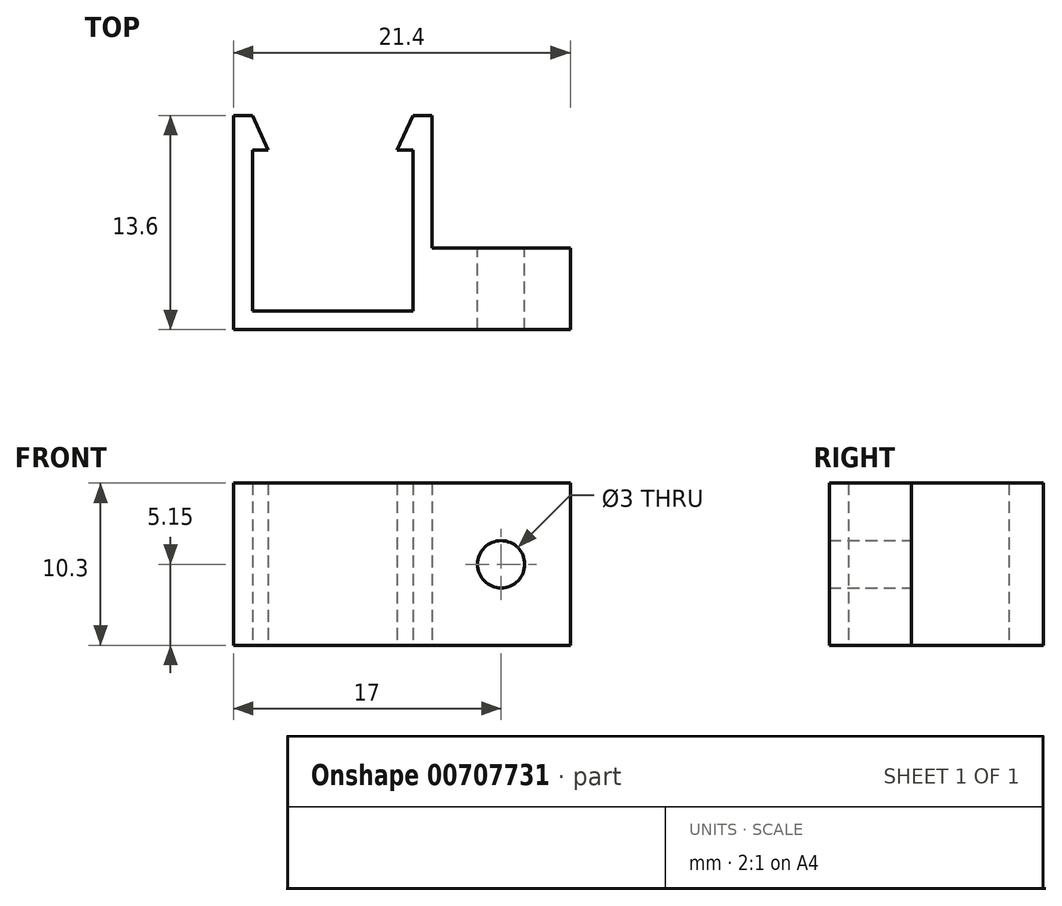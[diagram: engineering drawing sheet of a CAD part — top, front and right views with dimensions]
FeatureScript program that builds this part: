
annotation { "Feature Type Name" : "Feature", "Feature Type Description" : "" }
export const myFeature = defineFeature(function(context is Context, id is Id, definition is map)
    precondition{}
    {
        {
            var Q0;
            Q0=qCreatedBy(makeId("Top.planeOp"),FACE);
            var sketch = newSketch(context, id + "F0", { "sketchPlane" : qUnion([Q0])});
            skLineSegment(sketch, "E0.bottom", {"start": v(0, 0) * mm, "end": v(10.2, 0) * mm});
            skLineSegment(sketch, "E0.top", {"start": v(0, 10.2) * mm, "end": v(1, 10.2) * mm});
            skLineSegment(sketch, "E0.left", {"start": v(0, 0) * mm, "end": v(0, 10.2) * mm});
            skLineSegment(sketch, "E0.right", {"start": v(10.2, 0) * mm, "end": v(10.2, 10.2) * mm});
            skLineSegment(sketch, "E1.bottom", {"start": v(-1.2, 12.4) * mm, "end": v(0, 12.4) * mm});
            skLineSegment(sketch, "E1.top", {"start": v(-1.2, -1.2) * mm, "end": v(11.4, -1.2) * mm});
            skLineSegment(sketch, "E1.left", {"start": v(-1.2, 12.4) * mm, "end": v(-1.2, -1.2) * mm});
            skLineSegment(sketch, "E1.right", {"start": v(11.4, 12.4) * mm, "end": v(11.4, 4) * mm});
            skPoint(sketch, "E2", {"position": v(1, 10.2) * mm});
            skPoint(sketch, "E3", {"position": v(9.2, 10.2) * mm});
            skPoint(sketch, "E4", {"position": v(0, 12.4) * mm});
            skPoint(sketch, "E5", {"position": v(10.2, 12.4) * mm});
            skLineSegment(sketch, "E6", {"start": v(0, 12.4) * mm, "end": v(1, 10.2) * mm});
            skLineSegment(sketch, "E7", {"start": v(9.2, 10.2) * mm, "end": v(10.2, 12.4) * mm});
            skLineSegment(sketch, "E8.trimOffspring", {"start": v(10.2, 12.4) * mm, "end": v(11.4, 12.4) * mm});
            skLineSegment(sketch, "E9.trimOffspring", {"start": v(9.2, 10.2) * mm, "end": v(10.2, 10.2) * mm});
            skLineSegment(sketch, "E10.bottom", {"start": v(11.4, -1.2) * mm, "end": v(20.2, -1.2) * mm});
            skLineSegment(sketch, "E10.top", {"start": v(11.4, 4) * mm, "end": v(20.2, 4) * mm});
            skLineSegment(sketch, "E10.right", {"start": v(20.2, -1.2) * mm, "end": v(20.2, 4) * mm});
            skSolve(sketch);
        }
        {
            var Q0;
            Q0=makeQuery(id+"F0.imprint","IMPRINT",FACE,{"disambiguationData":[TD([[makeQuery(id+"F0.imprint","IMPRINT",EDGE,{"derivedFrom":sQuery(id+"F0.wireOp",EDGE,"E0.bottom")}),-1.0]])]});
            extrude(context, id + "F1", {"entities" : qUnion([Q0]), "depth" : 10.3 * mm, "offsetDistance" : 25 * mm});
        }
        {
            var Q0;
            Q0=makeQuery(id+"F1.opExtrude","SWEPT_FACE",FACE,{"disambiguationData":[OSD([sQuery(id+"F0.wireOp",EDGE,"E10.top")])]});
            var sketch = newSketch(context, id + "F2", { "sketchPlane" : qUnion([Q0])});
            skPoint(sketch, "E11", {"position": v(-15.8, 5.15) * mm});
            skPoint(sketch, "E11.positionSnap0", {"position": v(-15.8, 10.3) * mm});
            skPoint(sketch, "E11.positionSnap1", {"position": v(-20.2, 5.15) * mm});
            skSolve(sketch);
        }
        {
            var Q0;
            Q0=sQuery(id+"F2.wireOp",VERTEX,"E11");
            var Q1;
            Q1=makeQuery(id+"F1.opExtrude","SWEPT_BODY",BODY,{"disambiguationData":[OSD([sQuery(id+"F0.wireOp",EDGE,"E0.bottom"),sQuery(id+"F0.wireOp",EDGE,"E0.top"),sQuery(id+"F0.wireOp",EDGE,"E0.left"),sQuery(id+"F0.wireOp",EDGE,"E0.right"),sQuery(id+"F0.wireOp",EDGE,"E1.bottom"),sQuery(id+"F0.wireOp",EDGE,"E1.top"),sQuery(id+"F0.wireOp",EDGE,"E1.left"),sQuery(id+"F0.wireOp",EDGE,"E1.right"),sQuery(id+"F0.wireOp",EDGE,"E6"),sQuery(id+"F0.wireOp",EDGE,"E7"),sQuery(id+"F0.wireOp",EDGE,"E8.trimOffspring"),sQuery(id+"F0.wireOp",EDGE,"E9.trimOffspring"),sQuery(id+"F0.wireOp",EDGE,"E10.bottom"),sQuery(id+"F0.wireOp",EDGE,"E10.top"),sQuery(id+"F0.wireOp",EDGE,"E10.right")])]});
            hole(context, id + "F3", {"style" : HoleStyle.SIMPLE, "endStyle" : HoleEndStyle.THROUGH, "holeDiameter" : 3 * mm, "majorDiameter" : 5 * mm, "isTappedThrough" : true, "tappedDepth" : 12 * mm, "tapClearance" : 3, "startFromSketch" : true, "locations" : qUnion([Q0]), "scope" : qUnion([Q1])});
        }
    });
